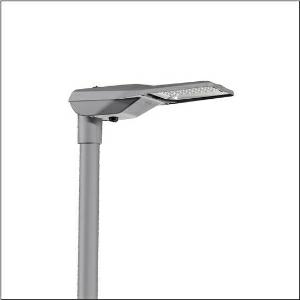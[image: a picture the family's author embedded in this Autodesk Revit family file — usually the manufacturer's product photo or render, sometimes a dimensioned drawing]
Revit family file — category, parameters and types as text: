
# Revit family: streetlight_sl_21_mini___stw1_0a_5xe2e43t08hb_75ae
name_source: partatom
category: Lighting Fixtures
units: mm (PartAtom-declared; Revit-internal decimal feet)

## family parameters
Cut with Voids When Loaded = No
Host = Face
Light Source = No
Part Type = Normal
Room Calculation Point = No
Round Connector Dimension = Use Diameter
Shared = No

## types (1)
- --- (1 x LED, 9430 lm, 66 W, 4000K)
    Apparent Load = 66 VA
    CIE Flux Codes = 38 75 98 100 100
    Color Rendering = 70
    Color Temperature = 4000K
    Default Elevation = 1800 mm
    Description = Streetlight SL 21 mini, mast luminaire, primary light control with lens, of PMMA, primary optical cover: cover, of toughened safety glass, transparent, light distribution: STW1.0a, light emission: direct distribution, primary light characteristic: asymmetric, installation type: side-entry, post-top, LED, High Power LED, rated luminous flux: 9.430lm, luminous efficacy: 143lm/W, light colour: 740, colour temperature: 4000K, control gear: D4i, control: overheat protection, constant luminous flux control, time-dependent luminous flux control, flexible luminous flux parameterisation, pre-setting: logarithmic dimming characteristic, mains connection: 220..240V, AC, 50/60Hz, start of lifetime: 66W, end of service life: 69W, reduction: 30W, luminaire housing, of diecast aluminium, powder-coated, SITECO metallic grey (DB 702S), corrosivity category C5 high according to DIN EN ISO 12944, please order mast flange separately, inclination adjustable: 0°, 5°, 10°, 15°, sealing non-destructively replaceable, multi-level sealing system, length: 628mm, width: 235mm, height: 110mm, mast flange for spigot size: 42mm (side-entry): 5XC10008XM4, 60/48mm (side-entry/post-top): 5XC10108XM2, 76/60mm (side-entry/post-top): 5XC10108XM1, mounting height: 4..8m, Smart Interface below and above, protection rating (complete): IP66, insulation class (complete): insulation class II (safety insulation), certification: CE, ENEC, ENEC+, VDE, impact resistance: IK10, permissible operating ambient temperature for outdoor applications: -40..+50°C, standard-compliant lighting for roads and squares, packaging unit: 1 piece

Light Distribution: STW1.0a
    Height = 110 mm
    Lamp = 1 x LED
    Lamp Light Flux = 9430 lm
    Lamp Power = 66 W
    Lamp count = 1
    Length = 625 mm
    Luminous efficacy = 143 lm/W
    Manufacturer = Siteco
    ModVariant = No
    Model = 5XE2E43T08HB
    Number of Poles = 1
    OnlyDefault = Yes
    Power Factor = 1
    Product Name = Streetlight SL 21 mini | STW1.0a
    Product group = mast luminaire | pylon top
    ProductGroupID = 6100
    Protection Class = Protection class II
    Protection Degree = IP 66
    RLX_Detail_Level = 1
    RLX_Emergency_Light_Flux = 0 lm
    RLX_Emergency_Type = 0
    RLX_Emergency_Type_DB = No
    RlxData = <blob elided: 26329 chars, md5=4afca9a8>
    Socket = socket
    Standby Power = 0 W
    System Light Flux = 9430 lm
    System Power = 66 W
    Type Comments = factory setting: luminous flux: 100 % | dim-lin: 254 | 670 mA
    Type Image = l_1003514.jpg
    URL = http://relux.com
    VarID = @adj_184615
    Voltage = 0 V
    Weight = 0.00 kg
    Width = 234 mm

## geometry (parser evidence)
native form markers: Blend x4, Sweep x13
no freeform markers — native parametric forms only
